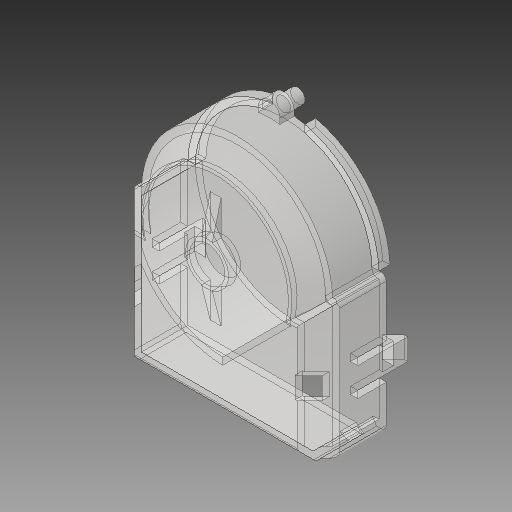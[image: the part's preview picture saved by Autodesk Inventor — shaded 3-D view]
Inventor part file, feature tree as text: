
AUTODESK INVENTOR PART (.ipt)
format: ipt  version: 2019 (Build 230136000, 136)  size: 245,760 bytes
history: mixed  units: mm
features: other x5, fillet x1, imported_body x1
ambient origin geometry x8: Origin, YZ Plane, XZ Plane, XY Plane, X Axis, Y Axis, Z Axis, Center Point
bodies: Body1 (imported_parasolid), Body2 (imported_parasolid), Body3 (imported_parasolid)
feature tree (7):
  other  "Твердое тело1"
  other  "Твердое тело2"
  other  "Твердое тело3"
  fillet  "Fillet3"  [1 undecoded]
  other  "Boss-Extrude37[1]"
  other  "Boss-Extrude37[2]"
  imported_body  NMx_Import_Brep_tag  [imported B-rep: ~70 faces, bbox_mm=[28.8, 34.559862, 9.71967]]
note: 1 required parameter value undecoded (feature->parameter linkage not recoverable at this tier; creation-order binding heuristic only, values carry confidence <= 0.55)
